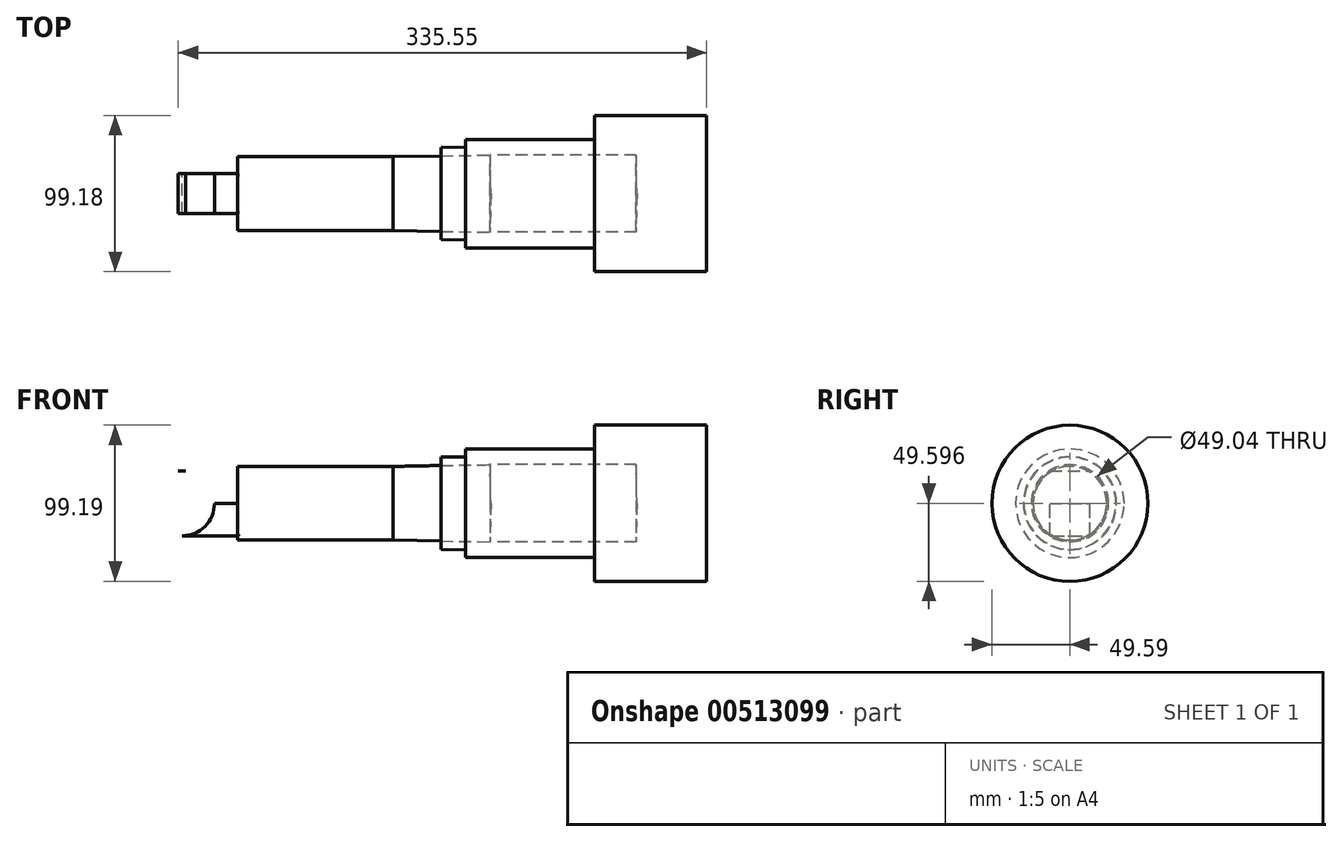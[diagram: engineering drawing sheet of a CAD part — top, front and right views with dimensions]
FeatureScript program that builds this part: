
annotation { "Feature Type Name" : "Feature", "Feature Type Description" : "" }
export const myFeature = defineFeature(function(context is Context, id is Id, definition is map)
    precondition{}
    {
        {
            var Q0;
            Q0=qCreatedBy(makeId("Front.planeOp"),FACE);
            var sketch = newSketch(context, id + "F0", { "sketchPlane" : qUnion([Q0])});
            skCircle(sketch, "E0", {"center": v(-134.2, 16.29) * mm, "radius": 20.67 * mm});
            skLineSegment(sketch, "E1", {"start": v(-136.51, 36.83) * mm, "end": v(-98.97, 36.83) * mm});
            skLineSegment(sketch, "E2", {"start": v(-134.2, -4.39) * mm, "end": v(-98.08, -4.39) * mm});
            skLineSegment(sketch, "E3", {"start": v(-98.08, -4.39) * mm, "end": v(-98.97, 39.68) * mm});
            skLineSegment(sketch, "E4", {"start": v(-98.97, 39.68) * mm, "end": v(0, 39.68) * mm});
            skLineSegment(sketch, "E5", {"start": v(0, 39.68) * mm, "end": v(30.43, 40.3) * mm});
            skLineSegment(sketch, "E6", {"start": v(30.43, 40.3) * mm, "end": v(30.91, 16.29) * mm});
            skLineSegment(sketch, "E7", {"start": v(61.52, 40.8) * mm, "end": v(62.01, 16.29) * mm});
            skLineSegment(sketch, "E8", {"start": v(30.43, 40.3) * mm, "end": v(61.52, 40.8) * mm});
            skCircle(sketch, "E9", {"center": v(236.24, 16.29) * mm, "radius": 20.67 * mm});
            skLineSegment(sketch, "E10", {"start": v(61.52, 40.8) * mm, "end": v(154.27, 40.8) * mm});
            skLineSegment(sketch, "E11", {"start": v(154.27, 40.8) * mm, "end": v(154.77, 16.29) * mm});
            skLineSegment(sketch, "E12", {"start": v(236.24, 36.96) * mm, "end": v(199.04, 36.96) * mm});
            skLineSegment(sketch, "E13", {"start": v(236.24, -4.39) * mm, "end": v(199.04, -4.39) * mm});
            skLineSegment(sketch, "E14", {"start": v(199.04, -4.39) * mm, "end": v(199.04, 36.96) * mm});
            skLineSegment(sketch, "E15", {"start": v(199.04, 36.96) * mm, "end": v(199.04, 65.88) * mm});
            skLineSegment(sketch, "E16", {"start": v(199.04, 65.88) * mm, "end": v(127.8, 65.88) * mm});
            skLineSegment(sketch, "E17", {"start": v(127.8, 65.88) * mm, "end": v(127.8, 50.74) * mm});
            skLineSegment(sketch, "E18", {"start": v(127.8, 50.74) * mm, "end": v(45.97, 50.74) * mm});
            skPoint(sketch, "E18.endSnap0", {"position": v(45.97, 40.55) * mm});
            skLineSegment(sketch, "E19", {"start": v(45.97, 50.74) * mm, "end": v(46.05, 45.82) * mm});
            skLineSegment(sketch, "E20", {"start": v(46.05, 45.82) * mm, "end": v(30.28, 45.56) * mm});
            skLineSegment(sketch, "E21", {"start": v(30.28, 45.56) * mm, "end": v(30.43, 40.3) * mm});
            skLineSegment(sketch, "E22", {"start": v(-134.2, 16.29) * mm, "end": v(-98.5, 16.29) * mm});
            skLineSegment(sketch, "E23", {"start": v(-98.5, 16.29) * mm, "end": v(30.91, 16.29) * mm});
            skLineSegment(sketch, "E24", {"start": v(62.01, 16.29) * mm, "end": v(154.77, 16.29) * mm});
            skLineSegment(sketch, "E25", {"start": v(199.04, 16.29) * mm, "end": v(236.24, 16.29) * mm});
            skLineSegment(sketch, "E26", {"start": v(30.91, 16.29) * mm, "end": v(62.01, 16.29) * mm});
            skLineSegment(sketch, "E27", {"start": v(154.77, 16.29) * mm, "end": v(199.04, 16.29) * mm});
            skSolve(sketch);
        }
        {
            var Q0;
            Q0=makeQuery(id+"F0.imprint","IMPRINT",FACE,{"disambiguationData":[TD([[makeQuery(id+"F0.imprint","IMPRINT",EDGE,{"derivedFrom":sQuery(id+"F0.wireOp",EDGE,"E8")}),1.0]])]});
            var Q1;
            Q1=sQuery(id+"F0.wireOp",EDGE,"E23");
            revolve(context, id + "F1", {"entities" : qUnion([Q0]), "axis" : qUnion([Q1]), "revolveType" : RevolveType.FULL});
        }
        {
            var Q0;
            {var subQ0=sQuery(id+"F0.wireOp",EDGE,"E4");Q0=makeQuery(id+"F0.imprint","IMPRINT",FACE,{"disambiguationData":[TD([[makeQuery(id+"F0.imprint","IMPRINT",EDGE,{"derivedFrom":subQ0}),-1.0]])]});}
            var Q1;
            Q1=makeQuery(id+"F0.imprint","IMPRINT",FACE,{"disambiguationData":[TD([[makeQuery(id+"F0.imprint","IMPRINT",EDGE,{"derivedFrom":sQuery(id+"F0.wireOp",EDGE,"E6")}),1.0]])]});
            var Q2;
            Q2=sQuery(id+"F0.wireOp",EDGE,"E23");
            revolve(context, id + "F2", {"entities" : qUnion([Q0, Q1]), "axis" : qUnion([Q2]), "revolveType" : RevolveType.FULL});
        }
        {
            var Q0;
            {var subQ0=sQuery(id+"F0.wireOp",EDGE,"E2");Q0=makeQuery(id+"F0.imprint","IMPRINT",FACE,{"disambiguationData":[TD([[makeQuery(id+"F0.imprint","IMPRINT",EDGE,{"derivedFrom":subQ0}),1.0]])]});}
            var Q1;
            {var subQ0=sQuery(id+"F0.wireOp",EDGE,"E1");var subQ1=sQuery(id+"F0.wireOp",EDGE,"E0");var subQ2=makeQuery(id+"F0.imprint","INTERSECT",VERTEX,{"disambiguationData":[OD(1.0)],"derivedFrom":[subQ1,subQ0]});Q1=makeQuery(id+"F0.imprint","IMPRINT",FACE,{"disambiguationData":[TD([[makeQuery(id+"F0.imprint","IMPRINT",EDGE,{"disambiguationData":[TD([[subQ2,1.0]])],"derivedFrom":subQ1}),1.0]])]});}
            extrude(context, id + "F3", {"entities" : qUnion([Q0, Q1]), "operationType" : NewBodyOperationType.ADD, "endBound" : BoundingType.SYMMETRIC, "depth" : 25.4 * mm, "offsetDistance" : 25.4 * mm});
        }
    });
